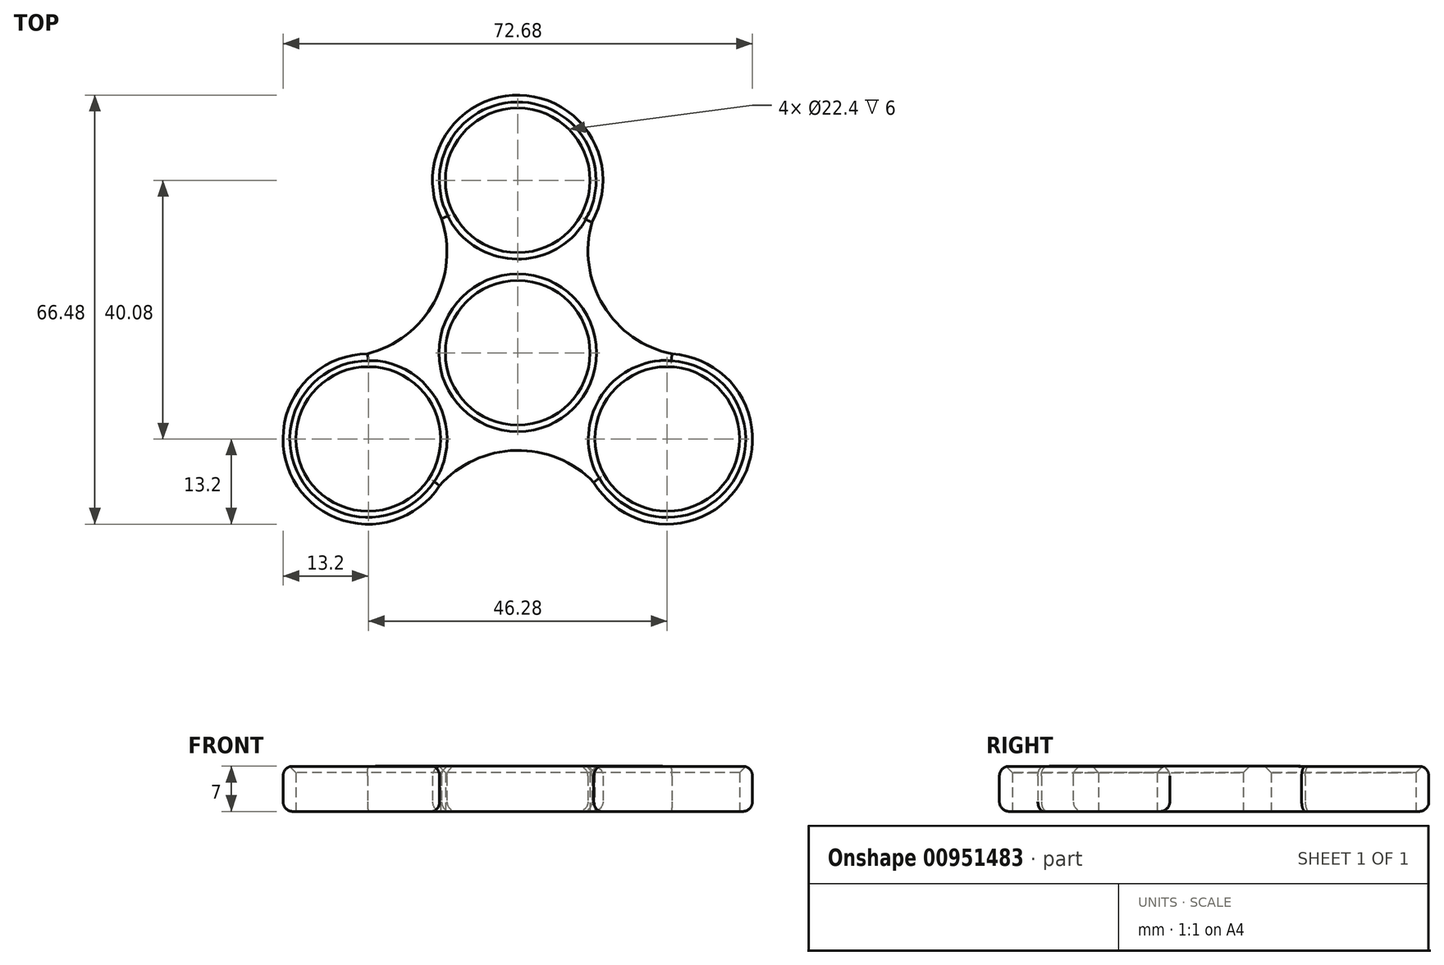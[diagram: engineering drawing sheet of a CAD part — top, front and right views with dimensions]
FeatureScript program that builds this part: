
annotation { "Feature Type Name" : "Feature", "Feature Type Description" : "" }
export const myFeature = defineFeature(function(context is Context, id is Id, definition is map)
    precondition{}
    {
        {
            var Q0;
            Q0=qCreatedBy(makeId("Top.planeOp"),FACE);
            var sketch = newSketch(context, id + "F0", { "sketchPlane" : qUnion([Q0])});
            skCircle(sketch, "E0", {"center": v(0, 0) * mm, "radius": 11.2 * mm});
            skCircle(sketch, "E1", {"center": v(0, 26.72) * mm, "radius": 11.2 * mm});
            skArc(sketch, "E2", {"start": v(11.5, 20.23) * mm, "mid": v(0.31, 39.92) * mm, "end": v(-11.8, 20.79) * mm});
            skArc(sketch, "E3.1.0", {"start": v(-23.27, -0.16) * mm, "mid": v(-34.73, -19.69) * mm, "end": v(-12.1, -20.6) * mm});
            skCircle(sketch, "E3.1.1", {"center": v(-23.14, -13.36) * mm, "radius": 11.2 * mm});
            skArc(sketch, "E3.2.0", {"start": v(11.77, -20.07) * mm, "mid": v(34.41, -20.23) * mm, "end": v(23.9, -0.18) * mm});
            skCircle(sketch, "E3.2.1", {"center": v(23.14, -13.36) * mm, "radius": 11.2 * mm});
            skArc(sketch, "E4", {"start": v(11.5, 20.23) * mm, "mid": v(13.25, 7.32) * mm, "end": v(23.9, -0.18) * mm});
            skArc(sketch, "E5.1.0", {"start": v(-23.27, -0.16) * mm, "mid": v(-12.96, 7.81) * mm, "end": v(-11.8, 20.79) * mm});
            skArc(sketch, "E5.2.0", {"start": v(11.77, -20.07) * mm, "mid": v(-0.28, -15.13) * mm, "end": v(-12.1, -20.6) * mm});
            skSolve(sketch);
        }
        {
            var Q0;
            Q0=makeQuery(id+"F0.imprint","IMPRINT",FACE,{"disambiguationData":[TD([[makeQuery(id+"F0.imprint","IMPRINT",EDGE,{"derivedFrom":sQuery(id+"F0.wireOp",EDGE,"E0")}),-1.0]])]});
            extrude(context, id + "F1", {"entities" : qUnion([Q0]), "depth" : 7 * mm, "offsetDistance" : 25 * mm});
        }
        {
            var Q0;
            Q0=makeQuery(id+"F1.opExtrude","CAP_EDGE",EDGE,{"disambiguationData":[OSD([sQuery(id+"F0.wireOp",EDGE,"E3.1.0")])],"isStart":false});
            var Q1;
            Q1=makeQuery(id+"F1.opExtrude","CAP_EDGE",EDGE,{"disambiguationData":[OSD([sQuery(id+"F0.wireOp",EDGE,"E5.2.0")])],"isStart":false});
            var Q2;
            Q2=makeQuery(id+"F1.opExtrude","CAP_EDGE",EDGE,{"disambiguationData":[OSD([sQuery(id+"F0.wireOp",EDGE,"E3.2.0")])],"isStart":false});
            var Q3;
            Q3=makeQuery(id+"F1.opExtrude","CAP_EDGE",EDGE,{"disambiguationData":[OSD([sQuery(id+"F0.wireOp",EDGE,"E4")])],"isStart":false});
            var Q4;
            Q4=makeQuery(id+"F1.opExtrude","CAP_EDGE",EDGE,{"disambiguationData":[OSD([sQuery(id+"F0.wireOp",EDGE,"E2")])],"isStart":false});
            var Q5;
            Q5=makeQuery(id+"F1.opExtrude","CAP_EDGE",EDGE,{"disambiguationData":[OSD([sQuery(id+"F0.wireOp",EDGE,"E5.1.0")])],"isStart":false});
            fillet(context, id + "F2", {"entities" : qUnion([Q0, Q1, Q2, Q3, Q4, Q5]), "radius" : 1.5 * mm, "tangentPropagation" : true, "allowEdgeOverflow" : false});
        }
        {
            var Q0;
            Q0=makeQuery(id+"F1.opExtrude","CAP_EDGE",EDGE,{"disambiguationData":[OSD([sQuery(id+"F0.wireOp",EDGE,"E5.2.0")])],"isStart":true});
            var Q1;
            Q1=makeQuery(id+"F1.opExtrude","CAP_EDGE",EDGE,{"disambiguationData":[OSD([sQuery(id+"F0.wireOp",EDGE,"E3.2.0")])],"isStart":true});
            var Q2;
            Q2=makeQuery(id+"F1.opExtrude","CAP_EDGE",EDGE,{"disambiguationData":[OSD([sQuery(id+"F0.wireOp",EDGE,"E4")])],"isStart":true});
            var Q3;
            Q3=makeQuery(id+"F1.opExtrude","CAP_EDGE",EDGE,{"disambiguationData":[OSD([sQuery(id+"F0.wireOp",EDGE,"E2")])],"isStart":true});
            var Q4;
            Q4=makeQuery(id+"F1.opExtrude","CAP_EDGE",EDGE,{"disambiguationData":[OSD([sQuery(id+"F0.wireOp",EDGE,"E5.1.0")])],"isStart":true});
            var Q5;
            Q5=makeQuery(id+"F1.opExtrude","CAP_EDGE",EDGE,{"disambiguationData":[OSD([sQuery(id+"F0.wireOp",EDGE,"E3.1.0")])],"isStart":true});
            fillet(context, id + "F3", {"entities" : qUnion([Q0, Q1, Q2, Q3, Q4, Q5]), "radius" : 1.5 * mm, "tangentPropagation" : true, "allowEdgeOverflow" : false});
        }
        {
            var Q0;
            Q0=makeQuery(id+"F1.opExtrude","CAP_EDGE",EDGE,{"disambiguationData":[OSD([sQuery(id+"F0.wireOp",EDGE,"E0")])],"isStart":false});
            var Q1;
            Q1=makeQuery(id+"F1.opExtrude","CAP_EDGE",EDGE,{"disambiguationData":[OSD([sQuery(id+"F0.wireOp",EDGE,"E1")])],"isStart":false});
            var Q2;
            Q2=makeQuery(id+"F1.opExtrude","CAP_EDGE",EDGE,{"disambiguationData":[OSD([sQuery(id+"F0.wireOp",EDGE,"E3.1.1")])],"isStart":false});
            var Q3;
            Q3=makeQuery(id+"F1.opExtrude","CAP_EDGE",EDGE,{"disambiguationData":[OSD([sQuery(id+"F0.wireOp",EDGE,"E3.2.1")])],"isStart":false});
            chamfer(context, id + "F4", {"entities" : qUnion([Q0, Q1, Q2, Q3]), "width" : 1 * mm, "tangentPropagation" : true});
        }
    });
